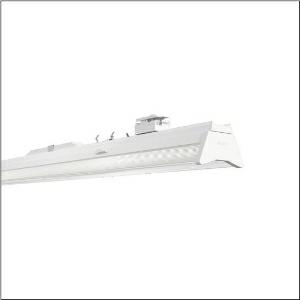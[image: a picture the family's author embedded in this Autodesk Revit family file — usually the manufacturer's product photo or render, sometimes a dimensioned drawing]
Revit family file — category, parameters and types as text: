
# Revit family: licross_r__21_performance_mo_52tm16dn46xg_f566
name_source: partatom
category: Lighting Fixtures
units: mm (PartAtom-declared; Revit-internal decimal feet)

## family parameters
Cut with Voids When Loaded = No
Host = Face
Light Source = No
Part Type = Normal
Room Calculation Point = No
Round Connector Dimension = Use Diameter
Shared = No

## types (1)
- --- (1 x LED, 6000 lm, 32.7 W, 4000K)
    Apparent Load = 33 VA
    CIE Flux Codes = 66 88 96 79 100
    Color Rendering = 80
    Color Temperature = 4000K
    Default Elevation = 1800 mm
    Description = Licross® 21 Performance MO, luminaire insert, of sheet steel, galvanised, coil coated, white, length: 1.500mm, width: 120mm, height: 123mm, LED rated luminous flux: 6.000lm, light colour: 840, control gear: DALI 2, control gear: ECG DALI, with plug, 5-pole, with phase selection, mains connection: 220..240V, AC, 50/60Hz, halogen-free wiring, primary light control with lens, of plastic, primary optical cover: cover, of PMMA, light emission: direct/indirect distribution, primary light characteristic: symmetric, protection rating (complete): IP40, insulation class (complete): insulation class I (protective earthing), certification: CE, ENEC, UKCA, protection symbol: D if used in an environment without relevant dust loads with corresponding accessories, impact resistance: IK06, permissible ambient temperature for indoor applications: -25..+45°C, corresponds to IFS (International Featured Standards) requirements for safety and quality in the food industry, reducing of maximum allowable ambient temperature of 5°C with ceiling mounting, LABS conformity tested according to VDMA 24364:2018-05, packaging unit: 1 piece
    Height = 114 mm
    Lamp = 1 x LED
    Lamp Light Flux = 6000 lm
    Lamp Power = 32.7 W
    Lamp count = 1
    Length = 1500 mm
    Luminous efficacy = 183 lm/W
    Manufacturer = Siteco
    ModVariant = No
    Model = 52TM16DN46XG
    Mounting Place = Ceiling
    Mounting Type = Pendant
    Number of Poles = 1
    OnlyDefault = Yes
    Power Factor = 1
    Product Name = Licross® 21 Performance MO
    Product group = luminaire insert
    ProductGroupID = 902
    Protection Class = Protection class I
    Protection Degree = IP 40
    RLX_Detail_Level = 1
    RlxData = <blob elided: 33697 chars, md5=6ec9bf13>
    Socket = socket
    Standby Power = 0 W
    System Light Flux = 6000 lm
    System Power = 33 W
    Type Comments = factory setting: luminous flux: 100 % | dim-lin: 254 | 222 mA
    Type Image = l_1256138.jpg
    URL = http://relux.com
    VarID = @adj_039553
    Voltage = 0 V
    Weight = 0.00 kg
    Width = 120 mm

## geometry (parser evidence)
native form markers: Blend x4, Sweep x13
no freeform markers — native parametric forms only
